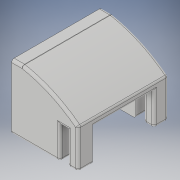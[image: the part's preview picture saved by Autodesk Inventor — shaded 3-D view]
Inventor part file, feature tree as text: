
AUTODESK INVENTOR PART (.ipt)
format: ipt  version: 2019 (Build 230136000, 136)  size: 484,864 bytes
history: native  units: in
note: dims shown in document units (in); Inventor stores cm internally (conversion verified against a paired STEP export)
features: extrude x22, sketch x22, fillet x11, other x4, reference x3, plane x2, projected_geometry x2
ambient origin geometry x8: Origin, YZ Plane, XZ Plane, XY Plane, X Axis, Y Axis, Z Axis, Center Point
bodies: Solid1 (feature_tree)
feature tree (66):
  extrude  "Extrusion1"  Depth=1.0in
  extrude  "Extrusion2"  Depth=0.95in TaperAngle=0.0deg
  extrude  "Extrusion3"  Depth=0.15in
  extrude  "Extrusion4"  Depth=0.15in
  extrude  "Extrusion5"  Depth=0.15in
  extrude  "Extrusion6"  Depth=0.2in TaperAngle=0.0deg
  extrude  "Extrusion7"  Depth=0.125in TaperAngle=0.0deg
  fillet  "Fillet1"  Radius=0.125in
  extrude  "Extrusion8"  Depth=0.03in TaperAngle=0.0deg
  plane  "Work Plane1"
  extrude  "Extrusion10"  Depth=0.03in TaperAngle=0.0deg
  extrude  "Extrusion11"  Depth=1.0in TaperAngle=0.0deg
  extrude  "Extrusion12"  Depth=1.0in TaperAngle=0.0deg
  extrude  "Extrusion13"  Depth=1.0in TaperAngle=0.0deg
  extrude  "Extrusion14"  Depth=1.0in
  extrude  "Extrusion15"  Depth=2.0in TaperAngle=0.0deg
  extrude  "Extrusion16"  Depth=0.07in TaperAngle=0.0deg
  extrude  "Extrusion17"  Depth=0.0394in
  extrude  "Extrusion18"  Depth=0.0394in
  extrude  "Extrusion19"  Depth=0.0394in
  extrude  "Extrusion20"  Depth=2.0in
  extrude  "Extrusion21"  Depth=0.0394in
  sketch  "Sketch24"  dims[d98=0.0394in d99=0.0394in d100=0.0394in]
  plane  "Work Plane2"
  extrude  "Extrusion22"  Depth=0.0394in
  fillet  "Fillet4"  Radius=0.0394in
  fillet  "Fillet5"  [1 undecoded]
  fillet  "Fillet6"  [1 undecoded]
  fillet  "Fillet10"  [1 undecoded]
  fillet  "Fillet12"  [1 undecoded]
  fillet  "Fillet13"  [1 undecoded]
  extrude  "Extrusion27"  [1 undecoded]
  fillet  "Fillet16"  [1 undecoded]
  fillet  "Fillet17"  [1 undecoded]
  fillet  "Fillet18"  [1 undecoded]
  fillet  "Fillet19"  [1 undecoded]
  sketch  "Sketch1"  dims[d0=1.0in d1=1.0in]
  sketch  "Sketch2"  dims[d2=1.0in d3=0.0in d7=0.95in d8=0.0in]
  sketch  "Sketch3"  dims[d9=0.15in d10=0.105in]
  sketch  "Sketch4"  dims[d11=1.075in d12=0.0in d13=0.15in]
  sketch  "Sketch5"  dims[d14=1.075in d15=0.0in d16=0.15in]
  sketch  "Sketch6"  dims[d17=0.2in d18=0.0in d19=0.2in d20=0.0in]
  sketch  "Sketch7"  dims[d21=0.19in d22=0.2625in d23=0.0in d24=0.125in]
  sketch  "Sketch8"  dims[d25=0.01in d26=0.0in d29=0.03in d30=0.0in]
  sketch  "Sketch11"  dims[d31=0.03in d32=0.0in d33=0.03in d34=0.0in]
  sketch  "Sketch12"  dims[d35=0.2175in d36=0.0in d37=1.0in d38=0.0in]
  sketch  "Sketch13"  dims[d39=1.0in d40=0.0in d41=1.0in d42=0.0in]
  sketch  "Sketch14"  dims[d43=1.0in d44=0.0in d45=1.0in d46=0.0in]
  sketch  "Sketch15"  dims[d47=1.0in d48=0.0in d49=0.0098in]
  sketch  "Sketch17"  dims[d50=0.0098in d51=2.0in d52=0.0in]
  projected_geometry  "Projected Loop1"
  sketch  "Sketch18"  dims[d53=0.07in d54=0.0in d55=0.07in d56=0.0in]
  sketch  "Sketch19"  dims[d74=0.0394in d75=0.0394in]
  reference  "Reference1"
  sketch  "Sketch20"  dims[d76=0.0394in d80=0.0394in]
  sketch  "Sketch21"  dims[d82=0.0394in d83=0.0394in]
  sketch  "Sketch22"  dims[d92=0.3937in d94=2.0in]
  reference  "Reference2"
  sketch  "Sketch23"  dims[d95=10.0in d96=0.0in d97=0.0394in]
  projected_geometry  "Projected Loop2"
  reference  "Reference3"
  sketch  "Sketch30"
  parser-record x1  (decoder bookkeeping rows leaked as tree rows — omitted from the tree; the rows remain in map.json)
  other  "AssemblyNEWarm.iam"
  other  "servo (2):1"
  other  "servo (2):2"
note: 10 required parameter values undecoded (feature->parameter linkage not recoverable at this tier; creation-order binding heuristic only, values carry confidence <= 0.55)
note: 1 file-system path scrubbed to <path> (originals preserved in map.json)
